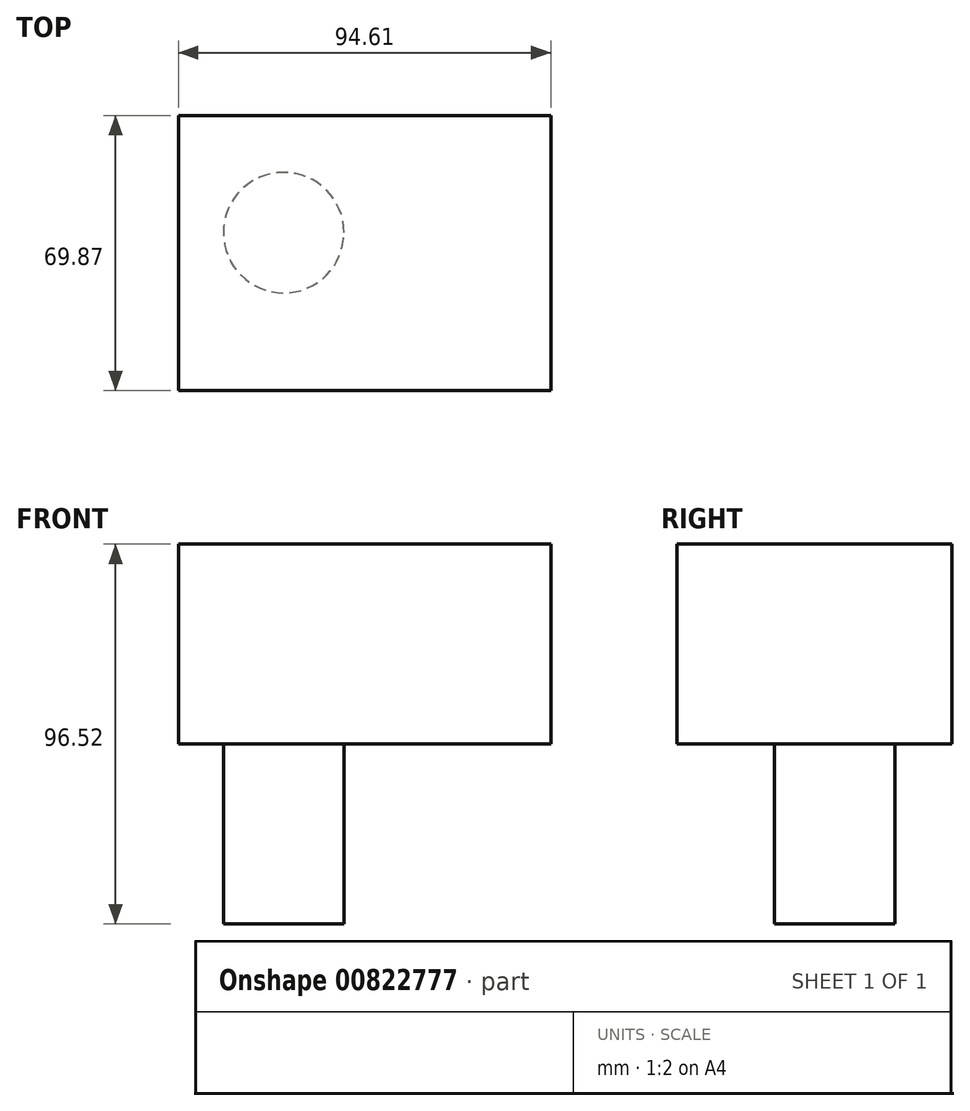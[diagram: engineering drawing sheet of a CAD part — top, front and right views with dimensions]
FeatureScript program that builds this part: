
annotation { "Feature Type Name" : "Feature", "Feature Type Description" : "" }
export const myFeature = defineFeature(function(context is Context, id is Id, definition is map)
    precondition{}
    {
        {
            var Q0;
            Q0=qCreatedBy(makeId("Top.planeOp"),FACE);
            var sketch = newSketch(context, id + "F0", { "sketchPlane" : qUnion([Q0])});
            skLineSegment(sketch, "E0.bottom", {"start": v(-132.02, 46.67) * mm, "end": v(-37.41, 46.67) * mm});
            skLineSegment(sketch, "E0.top", {"start": v(-132.02, -23.2) * mm, "end": v(-37.41, -23.2) * mm});
            skLineSegment(sketch, "E0.left", {"start": v(-132.02, 46.67) * mm, "end": v(-132.02, -23.2) * mm});
            skLineSegment(sketch, "E0.right", {"start": v(-37.41, 46.67) * mm, "end": v(-37.41, -23.2) * mm});
            skSolve(sketch);
        }
        {
            var Q0;
            Q0 = qSketchRegion(id + "F0", true);
            extrude(context, id + "F1", {"entities" : qUnion([Q0]), "depth" : 50.8 * mm, "offsetDistance" : 25.4 * mm});
        }
        {
            var Q0;
            Q0=makeQuery(id+"F1.opExtrude","CAP_FACE",FACE,{"disambiguationData":[OSD([sQuery(id+"F0.wireOp",EDGE,"E0.bottom"),sQuery(id+"F0.wireOp",EDGE,"E0.top"),sQuery(id+"F0.wireOp",EDGE,"E0.left"),sQuery(id+"F0.wireOp",EDGE,"E0.right")])],"isStart":false});
            var sketch = newSketch(context, id + "F2", { "sketchPlane" : qUnion([Q0])});
            skCircle(sketch, "E1", {"center": v(-105.26, 16.92) * mm, "radius": 15.32 * mm});
            skSolve(sketch);
        }
        {
            var Q0;
            Q0=makeQuery(id+"F2.imprint","IMPRINT",FACE,{"disambiguationData":[TD([[makeQuery(id+"F2.imprint","IMPRINT",EDGE,{"derivedFrom":sQuery(id+"F2.wireOp",EDGE,"E1")}),1.0]])]});
            extrude(context, id + "F3", {"entities" : qUnion([Q0]), "operationType" : NewBodyOperationType.ADD, "oppositeDirection" : true, "depth" : 96.52 * mm, "offsetDistance" : 25.4 * mm});
        }
    });
